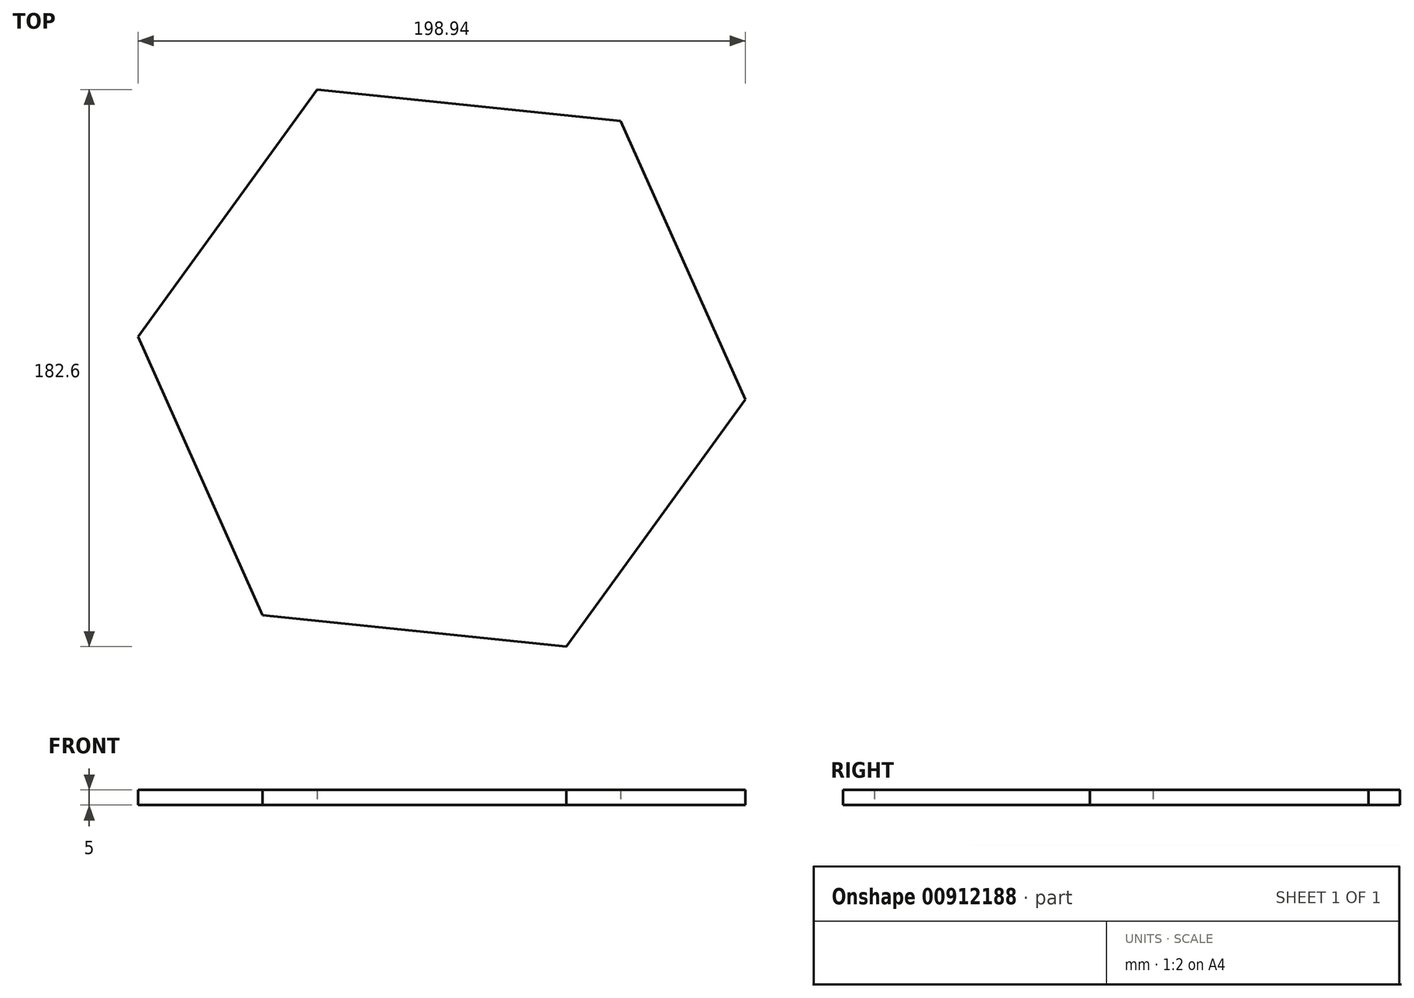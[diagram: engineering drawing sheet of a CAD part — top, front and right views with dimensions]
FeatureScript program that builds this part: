
annotation { "Feature Type Name" : "Feature", "Feature Type Description" : "" }
export const myFeature = defineFeature(function(context is Context, id is Id, definition is map)
    precondition{}
    {
        {
            var Q0;
            Q0=qCreatedBy(makeId("Top.planeOp"),FACE);
            var sketch = newSketch(context, id + "F0", { "sketchPlane" : qUnion([Q0])});
            skCircle(sketch, "E0.cCircle", {"center": v(0, 0) * mm, "radius": 86.6 * mm, "construction": true});
            skLineSegment(sketch, "E0.0", {"start": v(58.67, 80.98) * mm, "end": v(99.47, -10.32) * mm});
            skLineSegment(sketch, "E0.1", {"start": v(99.47, -10.32) * mm, "end": v(40.8, -91.3) * mm});
            skLineSegment(sketch, "E0.2", {"start": v(40.8, -91.3) * mm, "end": v(-58.67, -80.98) * mm});
            skLineSegment(sketch, "E0.3", {"start": v(-58.67, -80.98) * mm, "end": v(-99.47, 10.32) * mm});
            skLineSegment(sketch, "E0.4", {"start": v(-99.47, 10.32) * mm, "end": v(-40.8, 91.3) * mm});
            skLineSegment(sketch, "E0.5", {"start": v(-40.8, 91.3) * mm, "end": v(58.67, 80.98) * mm});
            skPoint(sketch, "E0.0.midPoint", {"position": v(79.07, 35.33) * mm});
            skSolve(sketch);
        }
        {
            var Q0;
            Q0=makeQuery(id+"F0.imprint","IMPRINT",FACE,{"disambiguationData":[TD([[makeQuery(id+"F0.imprint","IMPRINT",EDGE,{"derivedFrom":sQuery(id+"F0.wireOp",EDGE,"E0.0")}),-1.0]])]});
            extrude(context, id + "F1", {"entities" : qUnion([Q0]), "depth" : 5 * mm, "offsetDistance" : 25 * mm});
        }
    });
